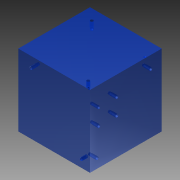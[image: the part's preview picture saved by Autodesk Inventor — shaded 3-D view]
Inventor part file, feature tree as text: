
AUTODESK INVENTOR PART (.ipt)
format: ipt  version: 2014 (Build 180170000, 170)  size: 213,504 bytes
history: native  units: mm
features: other x50, sketch x13, extrude x11
ambient origin geometry x8: Origin, YZ Plane, XZ Plane, XY Plane, X Axis, Y Axis, Z Axis, Center Point
bodies: 实体1 (feature_tree)
feature tree (74):
  extrude  "拉伸1"  Depth=14.0mm
  other  "UCS1"
  other  "UCS2"
  other  "UCS3"
  other  "UCS4"
  other  "UCS5"
  other  "UCS6"
  extrude  "拉伸2"  Depth=50.0mm
  extrude  "拉伸3"  Depth=44.0mm
  extrude  "拉伸4"  Depth=44.0mm
  extrude  "拉伸5"  Depth=32.0mm
  extrude  "拉伸6"  Depth=50.0mm
  extrude  "拉伸7"  Depth=32.0mm
  extrude  "拉伸8"  Depth=44.0mm TaperAngle=0.0deg
  extrude  "拉伸9"  Depth=44.0mm
  extrude  "拉伸10"  Depth=44.0mm
  extrude  "拉伸11"  Depth=44.0mm
  other  "iFeature11:6"
  other  "iFeature11:7"
  sketch  "草图1"  dims[d0=400.0mm d1=0.0mm]
  sketch  "草图2"  dims[d2=0.0mm d3=0.0mm d4=0.0mm d5=0.0mm d6=0.0mm d7=0.0mm]
  sketch  "草图3"  dims[d8=0.0mm d9=0.0mm d10=0.0mm d11=0.0mm d12=0.0mm d13=0.0mm]
  sketch  "草图4"  dims[d14=0.0mm d15=0.0mm d16=0.0mm d17=0.0mm d18=0.0mm d19=0.0mm]
  sketch  "草图5"  dims[d20=0.0mm d21=0.0mm d22=0.0mm d23=0.0mm d24=0.0mm d25=0.0mm]
  sketch  "草图6"  dims[d26=0.0mm d27=0.0mm d28=0.0mm d29=0.0mm d30=0.0mm d31=0.0mm]
  sketch  "草图7"  dims[d32=0.0mm d33=0.0mm d34=0.0mm d35=0.0mm d36=0.0mm d37=0.0mm d38=14.0mm]
  sketch  "草图8"  dims[d39=40.0mm d40=50.0mm]
  sketch  "草图9"  dims[d43=44.0mm d44=0.0mm d45=44.0mm d46=-10.297443mm]
  sketch  "草图10"  dims[d47=44.0mm d48=-10.297443mm d49=16.0mm]
  sketch  "草图11"  dims[d50=32.0mm d51=0.0mm d52=14.0mm]
  other  "UCS1: YZ 平面"
  other  "UCS1: XZ 平面"
  other  "UCS1: XY 平面"
  other  "UCS1: X 轴"
  other  "UCS1: Y 轴"
  other  "UCS1: Z 轴"
  other  "UCS1: 原点"
  other  "UCS2: YZ 平面"
  other  "UCS2: XZ 平面"
  other  "UCS2: XY 平面"
  other  "UCS2: X 轴"
  other  "UCS2: Y 轴"
  other  "UCS2: Z 轴"
  other  "UCS2: 原点"
  other  "UCS3: YZ 平面"
  other  "UCS3: XZ 平面"
  other  "UCS3: XY 平面"
  other  "UCS3: X 轴"
  other  "UCS3: Y 轴"
  other  "UCS3: Z 轴"
  other  "UCS3: 原点"
  other  "UCS4: YZ 平面"
  other  "UCS4: XZ 平面"
  other  "UCS4: XY 平面"
  other  "UCS4: X 轴"
  other  "UCS4: Y 轴"
  other  "UCS4: Z 轴"
  other  "UCS4: 原点"
  other  "UCS5: YZ 平面"
  other  "UCS5: XZ 平面"
  other  "UCS5: XY 平面"
  other  "UCS5: X 轴"
  other  "UCS5: Y 轴"
  other  "UCS5: Z 轴"
  other  "UCS5: 原点"
  other  "UCS6: YZ 平面"
  other  "UCS6: XZ 平面"
  other  "UCS6: XY 平面"
  other  "UCS6: X 轴"
  other  "UCS6: Y 轴"
  other  "UCS6: Z 轴"
  other  "UCS6: 原点"
  sketch  "草图38"  dims[d53=200.0mm d54=50.0mm]
  sketch  "草图39"  dims[d55=100.0mm d56=90.0mm d57=44.0mm d58=0.0mm d59=44.0mm d60=-10.297443mm d61=44.0mm d62=-10.297443mm d63=44.0mm d64=-10.297443mm d65=44.0mm d66=-10.297443mm d67=16.0mm d68=32.0mm d69=0.0mm d95=60.0mm d96=70.0mm d202=40.0mm d203=50.0mm d204=14.0mm d205=60.0mm d206=70.0mm d207=40.0mm d208=50.0mm d209=14.0mm d210=60.0mm d211=70.0mm]
